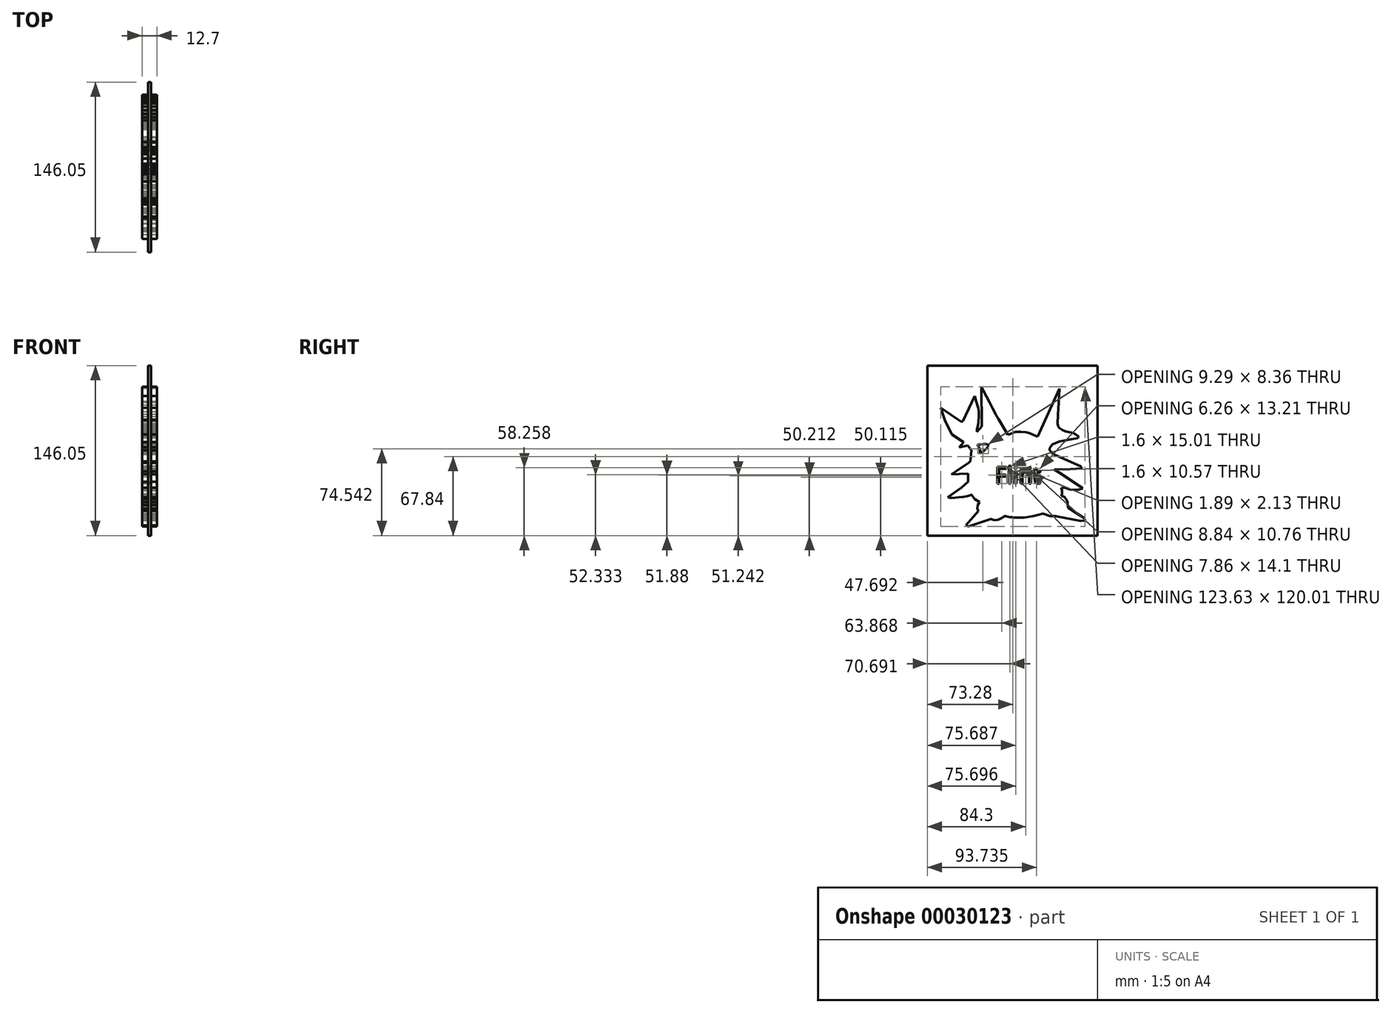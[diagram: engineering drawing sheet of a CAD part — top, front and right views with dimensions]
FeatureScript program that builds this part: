
annotation { "Feature Type Name" : "Feature", "Feature Type Description" : "" }
export const myFeature = defineFeature(function(context is Context, id is Id, definition is map)
    precondition{}
    {
        {
            var Q0;
            Q0=qCreatedBy(makeId("Right.planeOp"),FACE);
            var sketch = newSketch(context, id + "F0", { "sketchPlane" : qUnion([Q0])});
            skLineSegment(sketch, "E0", {"start": v(-27, 60) * mm, "end": v(-26.5, 59.02) * mm});
            skLineSegment(sketch, "E1", {"start": v(-26.5, 59.02) * mm, "end": v(-26.14, 58.34) * mm});
            skLineSegment(sketch, "E2", {"start": v(-26.14, 58.34) * mm, "end": v(-25.92, 57.91) * mm});
            skLineSegment(sketch, "E3", {"start": v(-25.92, 57.91) * mm, "end": v(-25.78, 57.65) * mm});
            skLineSegment(sketch, "E4", {"start": v(-25.78, 57.65) * mm, "end": v(-25.7, 57.5) * mm});
            skLineSegment(sketch, "E5", {"start": v(-25.7, 57.5) * mm, "end": v(-25.63, 57.36) * mm});
            skLineSegment(sketch, "E6", {"start": v(-25.63, 57.36) * mm, "end": v(-25.53, 57.18) * mm});
            skLineSegment(sketch, "E7", {"start": v(-25.53, 57.18) * mm, "end": v(-25.38, 56.88) * mm});
            skLineSegment(sketch, "E8", {"start": v(-25.38, 56.88) * mm, "end": v(-22.53, 51.43) * mm});
            skLineSegment(sketch, "E9", {"start": v(-22.53, 51.43) * mm, "end": v(-20, 46.58) * mm});
            skLineSegment(sketch, "E10", {"start": v(-20, 46.58) * mm, "end": v(-17.8, 42.37) * mm});
            skLineSegment(sketch, "E11", {"start": v(-17.8, 42.37) * mm, "end": v(-15.95, 38.84) * mm});
            skLineSegment(sketch, "E12", {"start": v(-15.95, 38.84) * mm, "end": v(-14.48, 36.03) * mm});
            skLineSegment(sketch, "E13", {"start": v(-14.48, 36.03) * mm, "end": v(-13.4, 33.98) * mm});
            skLineSegment(sketch, "E14", {"start": v(-13.4, 33.98) * mm, "end": v(-12.75, 32.72) * mm});
            skLineSegment(sketch, "E15", {"start": v(-12.75, 32.72) * mm, "end": v(-12.52, 32.29) * mm});
            skLineSegment(sketch, "E16", {"start": v(-12.52, 32.29) * mm, "end": v(-6.38, 22.2) * mm});
            skLineSegment(sketch, "E17", {"start": v(-6.38, 22.2) * mm, "end": v(-4.17, 18.74) * mm});
            skLineSegment(sketch, "E18", {"start": v(-4.17, 18.74) * mm, "end": v(-3.45, 19.08) * mm});
            skLineSegment(sketch, "E19", {"start": v(-3.45, 19.08) * mm, "end": v(-1.68, 19.86) * mm});
            skLineSegment(sketch, "E20", {"start": v(-1.68, 19.86) * mm, "end": v(0.54, 20.7) * mm});
            skLineSegment(sketch, "E21", {"start": v(0.54, 20.7) * mm, "end": v(2.6, 21.26) * mm});
            skLineSegment(sketch, "E22", {"start": v(2.6, 21.26) * mm, "end": v(6.85, 21.45) * mm});
            skLineSegment(sketch, "E23", {"start": v(6.85, 21.45) * mm, "end": v(11.1, 20.95) * mm});
            skLineSegment(sketch, "E24", {"start": v(11.1, 20.95) * mm, "end": v(12.86, 20.54) * mm});
            skLineSegment(sketch, "E25", {"start": v(12.86, 20.54) * mm, "end": v(14.77, 19.96) * mm});
            skLineSegment(sketch, "E26", {"start": v(14.77, 19.96) * mm, "end": v(16.3, 19.44) * mm});
            skLineSegment(sketch, "E27", {"start": v(16.3, 19.44) * mm, "end": v(16.93, 19.21) * mm});
            skLineSegment(sketch, "E28", {"start": v(16.93, 19.21) * mm, "end": v(21.34, 17) * mm});
            skLineSegment(sketch, "E29", {"start": v(21.34, 17) * mm, "end": v(39.92, 58.59) * mm});
            skLineSegment(sketch, "E30", {"start": v(39.92, 58.59) * mm, "end": v(39.45, 46.3) * mm});
            skLineSegment(sketch, "E31", {"start": v(39.45, 46.3) * mm, "end": v(38.82, 36.06) * mm});
            skLineSegment(sketch, "E32", {"start": v(38.82, 36.06) * mm, "end": v(38.5, 28.35) * mm});
            skLineSegment(sketch, "E33", {"start": v(38.5, 28.35) * mm, "end": v(38.58, 27.93) * mm});
            skLineSegment(sketch, "E34", {"start": v(38.58, 27.93) * mm, "end": v(38.8, 26.94) * mm});
            skLineSegment(sketch, "E35", {"start": v(38.8, 26.94) * mm, "end": v(39.2, 25.78) * mm});
            skLineSegment(sketch, "E36", {"start": v(39.2, 25.78) * mm, "end": v(39.77, 24.88) * mm});
            skLineSegment(sketch, "E37", {"start": v(39.77, 24.88) * mm, "end": v(42.43, 23.03) * mm});
            skLineSegment(sketch, "E38", {"start": v(42.43, 23.03) * mm, "end": v(45.44, 21.73) * mm});
            skLineSegment(sketch, "E39", {"start": v(45.44, 21.73) * mm, "end": v(48.6, 21.05) * mm});
            skLineSegment(sketch, "E40", {"start": v(48.6, 21.05) * mm, "end": v(51.74, 20.32) * mm});
            skLineSegment(sketch, "E41", {"start": v(51.74, 20.32) * mm, "end": v(54.1, 19.13) * mm});
            skLineSegment(sketch, "E42", {"start": v(54.1, 19.13) * mm, "end": v(56.15, 17.48) * mm});
            skLineSegment(sketch, "E43", {"start": v(56.15, 17.48) * mm, "end": v(56.38, 16.92) * mm});
            skLineSegment(sketch, "E44", {"start": v(56.38, 16.92) * mm, "end": v(56.24, 16.41) * mm});
            skLineSegment(sketch, "E45", {"start": v(56.24, 16.41) * mm, "end": v(55.97, 16.05) * mm});
            skLineSegment(sketch, "E46", {"start": v(55.97, 16.05) * mm, "end": v(55.83, 15.9) * mm});
            skLineSegment(sketch, "E47", {"start": v(55.83, 15.9) * mm, "end": v(50.16, 14.8) * mm});
            skLineSegment(sketch, "E48", {"start": v(50.16, 14.8) * mm, "end": v(40.08, 12.91) * mm});
            skLineSegment(sketch, "E49", {"start": v(40.08, 12.91) * mm, "end": v(34.1, 10.4) * mm});
            skLineSegment(sketch, "E50", {"start": v(34.1, 10.4) * mm, "end": v(31.9, 7.72) * mm});
            skLineSegment(sketch, "E51", {"start": v(31.9, 7.72) * mm, "end": v(31.58, 5.67) * mm});
            skLineSegment(sketch, "E52", {"start": v(31.58, 5.67) * mm, "end": v(33.47, 3.62) * mm});
            skLineSegment(sketch, "E53", {"start": v(33.47, 3.62) * mm, "end": v(35.36, 1.89) * mm});
            skLineSegment(sketch, "E54", {"start": v(35.36, 1.89) * mm, "end": v(35.99, 1.58) * mm});
            skLineSegment(sketch, "E55", {"start": v(35.99, 1.58) * mm, "end": v(58.2, -8.35) * mm});
            skLineSegment(sketch, "E56", {"start": v(58.2, -8.35) * mm, "end": v(59.3, -10.08) * mm});
            skLineSegment(sketch, "E57", {"start": v(59.3, -10.08) * mm, "end": v(49.22, -10.7) * mm});
            skLineSegment(sketch, "E58", {"start": v(49.22, -10.7) * mm, "end": v(35.67, -11.18) * mm});
            skLineSegment(sketch, "E59", {"start": v(35.67, -11.18) * mm, "end": v(39.6, -13.7) * mm});
            skLineSegment(sketch, "E60", {"start": v(39.6, -13.7) * mm, "end": v(59.45, -26.62) * mm});
            skLineSegment(sketch, "E61", {"start": v(59.45, -26.62) * mm, "end": v(60.08, -27.4) * mm});
            skLineSegment(sketch, "E62", {"start": v(60.08, -27.4) * mm, "end": v(55.99, -28.5) * mm});
            skLineSegment(sketch, "E63", {"start": v(55.99, -28.5) * mm, "end": v(49.37, -28.2) * mm});
            skLineSegment(sketch, "E64", {"start": v(49.37, -28.2) * mm, "end": v(45.28, -26.93) * mm});
            skLineSegment(sketch, "E65", {"start": v(45.28, -26.93) * mm, "end": v(41.5, -26.62) * mm});
            skLineSegment(sketch, "E66", {"start": v(41.5, -26.62) * mm, "end": v(42.13, -29.6) * mm});
            skLineSegment(sketch, "E67", {"start": v(42.13, -29.6) * mm, "end": v(42.13, -32.13) * mm});
            skLineSegment(sketch, "E68", {"start": v(42.13, -32.13) * mm, "end": v(41.66, -33.86) * mm});
            skLineSegment(sketch, "E69", {"start": v(41.66, -33.86) * mm, "end": v(41.93, -33.91) * mm});
            skLineSegment(sketch, "E70", {"start": v(41.93, -33.91) * mm, "end": v(42.59, -34.07) * mm});
            skLineSegment(sketch, "E71", {"start": v(42.59, -34.07) * mm, "end": v(43.37, -34.32) * mm});
            skLineSegment(sketch, "E72", {"start": v(43.37, -34.32) * mm, "end": v(44.02, -34.65) * mm});
            skLineSegment(sketch, "E73", {"start": v(44.02, -34.65) * mm, "end": v(45.62, -36.34) * mm});
            skLineSegment(sketch, "E74", {"start": v(45.62, -36.34) * mm, "end": v(46.7, -38.43) * mm});
            skLineSegment(sketch, "E75", {"start": v(46.7, -38.43) * mm, "end": v(46.9, -39.16) * mm});
            skLineSegment(sketch, "E76", {"start": v(46.9, -39.16) * mm, "end": v(47.04, -40.02) * mm});
            skLineSegment(sketch, "E77", {"start": v(47.04, -40.02) * mm, "end": v(47.12, -40.93) * mm});
            skLineSegment(sketch, "E78", {"start": v(47.12, -40.93) * mm, "end": v(47.17, -41.83) * mm});
            skLineSegment(sketch, "E79", {"start": v(47.17, -41.83) * mm, "end": v(47.19, -42.65) * mm});
            skLineSegment(sketch, "E80", {"start": v(47.19, -42.65) * mm, "end": v(47.18, -43.32) * mm});
            skLineSegment(sketch, "E81", {"start": v(47.18, -43.32) * mm, "end": v(47.17, -43.77) * mm});
            skLineSegment(sketch, "E82", {"start": v(47.17, -43.77) * mm, "end": v(47.17, -43.94) * mm});
            skLineSegment(sketch, "E83", {"start": v(47.17, -43.94) * mm, "end": v(61.81, -53.39) * mm});
            skLineSegment(sketch, "E84", {"start": v(61.81, -53.39) * mm, "end": v(61.66, -54.96) * mm});
            skLineSegment(sketch, "E85", {"start": v(61.66, -54.96) * mm, "end": v(58.2, -55.12) * mm});
            skLineSegment(sketch, "E86", {"start": v(58.2, -55.12) * mm, "end": v(38.03, -51.34) * mm});
            skLineSegment(sketch, "E87", {"start": v(38.03, -51.34) * mm, "end": v(36.93, -51.18) * mm});
            skLineSegment(sketch, "E88", {"start": v(36.93, -51.18) * mm, "end": v(32.2, -51.18) * mm});
            skLineSegment(sketch, "E89", {"start": v(32.2, -51.18) * mm, "end": v(25.6, -48.82) * mm});
            skLineSegment(sketch, "E90", {"start": v(25.6, -48.82) * mm, "end": v(24.72, -49.12) * mm});
            skLineSegment(sketch, "E91", {"start": v(24.72, -49.12) * mm, "end": v(22.6, -49.81) * mm});
            skLineSegment(sketch, "E92", {"start": v(22.6, -49.81) * mm, "end": v(19.97, -50.6) * mm});
            skLineSegment(sketch, "E93", {"start": v(19.97, -50.6) * mm, "end": v(17.56, -51.18) * mm});
            skLineSegment(sketch, "E94", {"start": v(17.56, -51.18) * mm, "end": v(9.87, -52.23) * mm});
            skLineSegment(sketch, "E95", {"start": v(9.87, -52.23) * mm, "end": v(2.13, -52.44) * mm});
            skLineSegment(sketch, "E96", {"start": v(2.13, -52.44) * mm, "end": v(0.8, -52.35) * mm});
            skLineSegment(sketch, "E97", {"start": v(0.8, -52.35) * mm, "end": v(-0.7, -52.18) * mm});
            skLineSegment(sketch, "E98", {"start": v(-0.7, -52.18) * mm, "end": v(-2.26, -51.95) * mm});
            skLineSegment(sketch, "E99", {"start": v(-2.26, -51.95) * mm, "end": v(-3.8, -51.7) * mm});
            skLineSegment(sketch, "E100", {"start": v(-3.8, -51.7) * mm, "end": v(-5.17, -51.45) * mm});
            skLineSegment(sketch, "E101", {"start": v(-5.17, -51.45) * mm, "end": v(-6.3, -51.23) * mm});
            skLineSegment(sketch, "E102", {"start": v(-6.3, -51.23) * mm, "end": v(-7.05, -51.08) * mm});
            skLineSegment(sketch, "E103", {"start": v(-7.05, -51.08) * mm, "end": v(-7.32, -51.03) * mm});
            skLineSegment(sketch, "E104", {"start": v(-7.32, -51.03) * mm, "end": v(-7.4, -51.1) * mm});
            skLineSegment(sketch, "E105", {"start": v(-7.4, -51.1) * mm, "end": v(-7.65, -51.32) * mm});
            skLineSegment(sketch, "E106", {"start": v(-7.65, -51.32) * mm, "end": v(-8, -51.63) * mm});
            skLineSegment(sketch, "E107", {"start": v(-8, -51.63) * mm, "end": v(-8.45, -52) * mm});
            skLineSegment(sketch, "E108", {"start": v(-8.45, -52) * mm, "end": v(-8.95, -52.4) * mm});
            skLineSegment(sketch, "E109", {"start": v(-8.95, -52.4) * mm, "end": v(-9.48, -52.79) * mm});
            skLineSegment(sketch, "E110", {"start": v(-9.48, -52.79) * mm, "end": v(-10, -53.13) * mm});
            skLineSegment(sketch, "E111", {"start": v(-10, -53.13) * mm, "end": v(-10.47, -53.39) * mm});
            skLineSegment(sketch, "E112", {"start": v(-10.47, -53.39) * mm, "end": v(-13.01, -54.24) * mm});
            skLineSegment(sketch, "E113", {"start": v(-13.01, -54.24) * mm, "end": v(-15.67, -54.5) * mm});
            skLineSegment(sketch, "E114", {"start": v(-15.67, -54.5) * mm, "end": v(-16.67, -54.33) * mm});
            skLineSegment(sketch, "E115", {"start": v(-16.67, -54.33) * mm, "end": v(-17.75, -54) * mm});
            skLineSegment(sketch, "E116", {"start": v(-17.75, -54) * mm, "end": v(-18.62, -53.69) * mm});
            skLineSegment(sketch, "E117", {"start": v(-18.62, -53.69) * mm, "end": v(-18.98, -53.55) * mm});
            skLineSegment(sketch, "E118", {"start": v(-18.98, -53.55) * mm, "end": v(-38.2, -60) * mm});
            skLineSegment(sketch, "E119", {"start": v(-38.2, -60) * mm, "end": v(-40.4, -59.06) * mm});
            skLineSegment(sketch, "E120", {"start": v(-40.4, -59.06) * mm, "end": v(-29.37, -46.77) * mm});
            skLineSegment(sketch, "E121", {"start": v(-29.37, -46.77) * mm, "end": v(-30.32, -44.73) * mm});
            skLineSegment(sketch, "E122", {"start": v(-30.32, -44.73) * mm, "end": v(-30, -41.58) * mm});
            skLineSegment(sketch, "E123", {"start": v(-30, -41.58) * mm, "end": v(-28.58, -39.06) * mm});
            skLineSegment(sketch, "E124", {"start": v(-28.58, -39.06) * mm, "end": v(-32.52, -36.38) * mm});
            skLineSegment(sketch, "E125", {"start": v(-32.52, -36.38) * mm, "end": v(-35.51, -32.6) * mm});
            skLineSegment(sketch, "E126", {"start": v(-35.51, -32.6) * mm, "end": v(-35.9, -32.78) * mm});
            skLineSegment(sketch, "E127", {"start": v(-35.9, -32.78) * mm, "end": v(-36.85, -33.2) * mm});
            skLineSegment(sketch, "E128", {"start": v(-36.85, -33.2) * mm, "end": v(-38.04, -33.66) * mm});
            skLineSegment(sketch, "E129", {"start": v(-38.04, -33.66) * mm, "end": v(-39.14, -34.02) * mm});
            skLineSegment(sketch, "E130", {"start": v(-39.14, -34.02) * mm, "end": v(-42.66, -34.53) * mm});
            skLineSegment(sketch, "E131", {"start": v(-42.66, -34.53) * mm, "end": v(-46.22, -34.8) * mm});
            skLineSegment(sketch, "E132", {"start": v(-46.22, -34.8) * mm, "end": v(-49.3, -35.23) * mm});
            skLineSegment(sketch, "E133", {"start": v(-49.3, -35.23) * mm, "end": v(-52.37, -35.43) * mm});
            skLineSegment(sketch, "E134", {"start": v(-52.37, -35.43) * mm, "end": v(-53.45, -35.32) * mm});
            skLineSegment(sketch, "E135", {"start": v(-53.45, -35.32) * mm, "end": v(-54.64, -35.1) * mm});
            skLineSegment(sketch, "E136", {"start": v(-54.64, -35.1) * mm, "end": v(-55.6, -34.9) * mm});
            skLineSegment(sketch, "E137", {"start": v(-55.6, -34.9) * mm, "end": v(-55.99, -34.8) * mm});
            skLineSegment(sketch, "E138", {"start": v(-55.99, -34.8) * mm, "end": v(-44.02, -26.62) * mm});
            skLineSegment(sketch, "E139", {"start": v(-44.02, -26.62) * mm, "end": v(-38.35, -21.58) * mm});
            skLineSegment(sketch, "E140", {"start": v(-38.35, -21.58) * mm, "end": v(-38.5, -14.49) * mm});
            skLineSegment(sketch, "E141", {"start": v(-38.5, -14.49) * mm, "end": v(-46.07, -14.8) * mm});
            skLineSegment(sketch, "E142", {"start": v(-46.07, -14.8) * mm, "end": v(-52.68, -15.12) * mm});
            skLineSegment(sketch, "E143", {"start": v(-52.68, -15.12) * mm, "end": v(-48.74, -12.76) * mm});
            skLineSegment(sketch, "E144", {"start": v(-48.74, -12.76) * mm, "end": v(-38.03, -5.51) * mm});
            skLineSegment(sketch, "E145", {"start": v(-38.03, -5.51) * mm, "end": v(-36.46, -4.1) * mm});
            skLineSegment(sketch, "E146", {"start": v(-36.46, -4.1) * mm, "end": v(-35.67, 5.36) * mm});
            skLineSegment(sketch, "E147", {"start": v(-35.67, 5.36) * mm, "end": v(-38.66, 9.45) * mm});
            skLineSegment(sketch, "E148", {"start": v(-38.66, 9.45) * mm, "end": v(-45.9, 8.03) * mm});
            skLineSegment(sketch, "E149", {"start": v(-45.9, 8.03) * mm, "end": v(-42.13, 12.28) * mm});
            skLineSegment(sketch, "E150", {"start": v(-42.13, 12.28) * mm, "end": v(-52.37, 19.06) * mm});
            skLineSegment(sketch, "E151", {"start": v(-52.37, 19.06) * mm, "end": v(-58.35, 31.34) * mm});
            skLineSegment(sketch, "E152", {"start": v(-58.35, 31.34) * mm, "end": v(-61.81, 42.05) * mm});
            skLineSegment(sketch, "E153", {"start": v(-61.81, 42.05) * mm, "end": v(-44.18, 29.92) * mm});
            skLineSegment(sketch, "E154", {"start": v(-44.18, 29.92) * mm, "end": v(-42.92, 30.55) * mm});
            skLineSegment(sketch, "E155", {"start": v(-42.92, 30.55) * mm, "end": v(-32.52, 51.97) * mm});
            skLineSegment(sketch, "E156", {"start": v(-32.52, 51.97) * mm, "end": v(-31.26, 47.25) * mm});
            skLineSegment(sketch, "E157", {"start": v(-31.26, 47.25) * mm, "end": v(-30.98, 46.31) * mm});
            skLineSegment(sketch, "E158", {"start": v(-30.98, 46.31) * mm, "end": v(-30.35, 44.02) * mm});
            skLineSegment(sketch, "E159", {"start": v(-30.35, 44.02) * mm, "end": v(-29.66, 41.19) * mm});
            skLineSegment(sketch, "E160", {"start": v(-29.66, 41.19) * mm, "end": v(-29.21, 38.59) * mm});
            skLineSegment(sketch, "E161", {"start": v(-29.21, 38.59) * mm, "end": v(-29.18, 34.18) * mm});
            skLineSegment(sketch, "E162", {"start": v(-29.18, 34.18) * mm, "end": v(-29.53, 29.77) * mm});
            skLineSegment(sketch, "E163", {"start": v(-29.53, 29.77) * mm, "end": v(-29.84, 27.09) * mm});
            skLineSegment(sketch, "E164", {"start": v(-29.84, 27.09) * mm, "end": v(-30.1, 26) * mm});
            skLineSegment(sketch, "E165", {"start": v(-30.1, 26) * mm, "end": v(-30.4, 24.82) * mm});
            skLineSegment(sketch, "E166", {"start": v(-30.4, 24.82) * mm, "end": v(-30.68, 23.86) * mm});
            skLineSegment(sketch, "E167", {"start": v(-30.68, 23.86) * mm, "end": v(-30.79, 23.47) * mm});
            skLineSegment(sketch, "E168", {"start": v(-30.79, 23.47) * mm, "end": v(-30.79, 21.26) * mm});
            skLineSegment(sketch, "E169", {"start": v(-30.79, 21.26) * mm, "end": v(-26.54, 26.14) * mm});
            skLineSegment(sketch, "E170", {"start": v(-26.54, 26.14) * mm, "end": v(-27, 60) * mm});
            skLineSegment(sketch, "E171", {"start": v(-28.27, 2.52) * mm, "end": v(-27.89, 2.78) * mm});
            skLineSegment(sketch, "E172", {"start": v(-27.89, 2.78) * mm, "end": v(-26.9, 3.48) * mm});
            skLineSegment(sketch, "E173", {"start": v(-26.9, 3.48) * mm, "end": v(-25.53, 4.5) * mm});
            skLineSegment(sketch, "E174", {"start": v(-25.53, 4.5) * mm, "end": v(-24.02, 5.7) * mm});
            skLineSegment(sketch, "E175", {"start": v(-24.02, 5.7) * mm, "end": v(-22.6, 7) * mm});
            skLineSegment(sketch, "E176", {"start": v(-22.6, 7) * mm, "end": v(-21.5, 8.23) * mm});
            skLineSegment(sketch, "E177", {"start": v(-21.5, 8.23) * mm, "end": v(-20.94, 9.3) * mm});
            skLineSegment(sketch, "E178", {"start": v(-20.94, 9.3) * mm, "end": v(-21.18, 10.08) * mm});
            skLineSegment(sketch, "E179", {"start": v(-21.18, 10.08) * mm, "end": v(-22.96, 10.81) * mm});
            skLineSegment(sketch, "E180", {"start": v(-22.96, 10.81) * mm, "end": v(-25.24, 10.88) * mm});
            skLineSegment(sketch, "E181", {"start": v(-25.24, 10.88) * mm, "end": v(-27.66, 10.63) * mm});
            skLineSegment(sketch, "E182", {"start": v(-27.66, 10.63) * mm, "end": v(-29.84, 10.4) * mm});
            skLineSegment(sketch, "E183", {"start": v(-29.84, 10.4) * mm, "end": v(-30.2, 10.26) * mm});
            skLineSegment(sketch, "E184", {"start": v(-30.2, 10.26) * mm, "end": v(-30.23, 9.94) * mm});
            skLineSegment(sketch, "E185", {"start": v(-30.23, 9.94) * mm, "end": v(-30.04, 9.48) * mm});
            skLineSegment(sketch, "E186", {"start": v(-30.04, 9.48) * mm, "end": v(-29.69, 8.91) * mm});
            skLineSegment(sketch, "E187", {"start": v(-29.69, 8.91) * mm, "end": v(-29.26, 8.3) * mm});
            skLineSegment(sketch, "E188", {"start": v(-29.26, 8.3) * mm, "end": v(-28.83, 7.65) * mm});
            skLineSegment(sketch, "E189", {"start": v(-28.83, 7.65) * mm, "end": v(-28.47, 7.02) * mm});
            skLineSegment(sketch, "E190", {"start": v(-28.47, 7.02) * mm, "end": v(-28.27, 6.46) * mm});
            skLineSegment(sketch, "E191", {"start": v(-28.27, 6.46) * mm, "end": v(-28.17, 5.3) * mm});
            skLineSegment(sketch, "E192", {"start": v(-28.17, 5.3) * mm, "end": v(-28.18, 4) * mm});
            skLineSegment(sketch, "E193", {"start": v(-28.18, 4) * mm, "end": v(-28.23, 2.95) * mm});
            skLineSegment(sketch, "E194", {"start": v(-28.23, 2.95) * mm, "end": v(-28.27, 2.52) * mm});
            skSolve(sketch);
        }
        {
            var Q0;
            Q0=makeQuery(id+"F0.imprint","IMPRINT",FACE,{"disambiguationData":[TD([[makeQuery(id+"F0.imprint","IMPRINT",EDGE,{"derivedFrom":sQuery(id+"F0.wireOp",EDGE,"E0")}),-1.0]])]});
            extrude(context, id + "F1", {"entities" : qUnion([Q0]), "endBound" : BoundingType.SYMMETRIC, "depth" : 12.7 * mm});
        }
        {
            var Q0;
            Q0=qCreatedBy(makeId("Right.planeOp"),FACE);
            var sketch = newSketch(context, id + "F2", { "sketchPlane" : qUnion([Q0])});
            skLineSegment(sketch, "E195.bottom", {"start": v(72.77, 78.2) * mm, "end": v(-73.28, 78.2) * mm});
            skLineSegment(sketch, "E195.top", {"start": v(72.77, -67.84) * mm, "end": v(-73.28, -67.84) * mm});
            skLineSegment(sketch, "E195.left", {"start": v(72.77, 78.2) * mm, "end": v(72.77, -67.84) * mm});
            skLineSegment(sketch, "E195.right", {"start": v(-73.28, 78.2) * mm, "end": v(-73.28, -67.84) * mm});
            skSolve(sketch);
        }
        {
            var Q0;
            Q0=makeQuery(id+"F2.imprint","IMPRINT",FACE,{"disambiguationData":[TD([[makeQuery(id+"F2.imprint","IMPRINT",EDGE,{"derivedFrom":sQuery(id+"F2.wireOp",EDGE,"E195.bottom")}),1.0]])]});
            extrude(context, id + "F3", {"entities" : qUnion([Q0]), "operationType" : NewBodyOperationType.ADD, "endBound" : BoundingType.SYMMETRIC, "depth" : 2.54 * mm});
        }
        {
            var Q0;
            Q0=qCreatedBy(makeId("Right.planeOp"),FACE);
            var sketch = newSketch(context, id + "F4", { "sketchPlane" : qUnion([Q0])});
            skText(sketch, "E196", { "text": "Flint\n", "fontName": "OpenSans-Regular.ttf"});
            const initialGuessF4  = {"E196": [-0.01528, -0.02301, 1, 0, 0.01422]};
            skSetInitialGuess(sketch, initialGuessF4);
            skSolve(sketch);
        }
        {
            var Q0;
            Q0 = qSketchRegion(id + "F4", true);
            extrude(context, id + "F5", {"entities" : qUnion([Q0]), "operationType" : NewBodyOperationType.REMOVE, "endBound" : BoundingType.SYMMETRIC, "oppositeDirection" : true, "depth" : 50.8 * mm});
        }
    });
